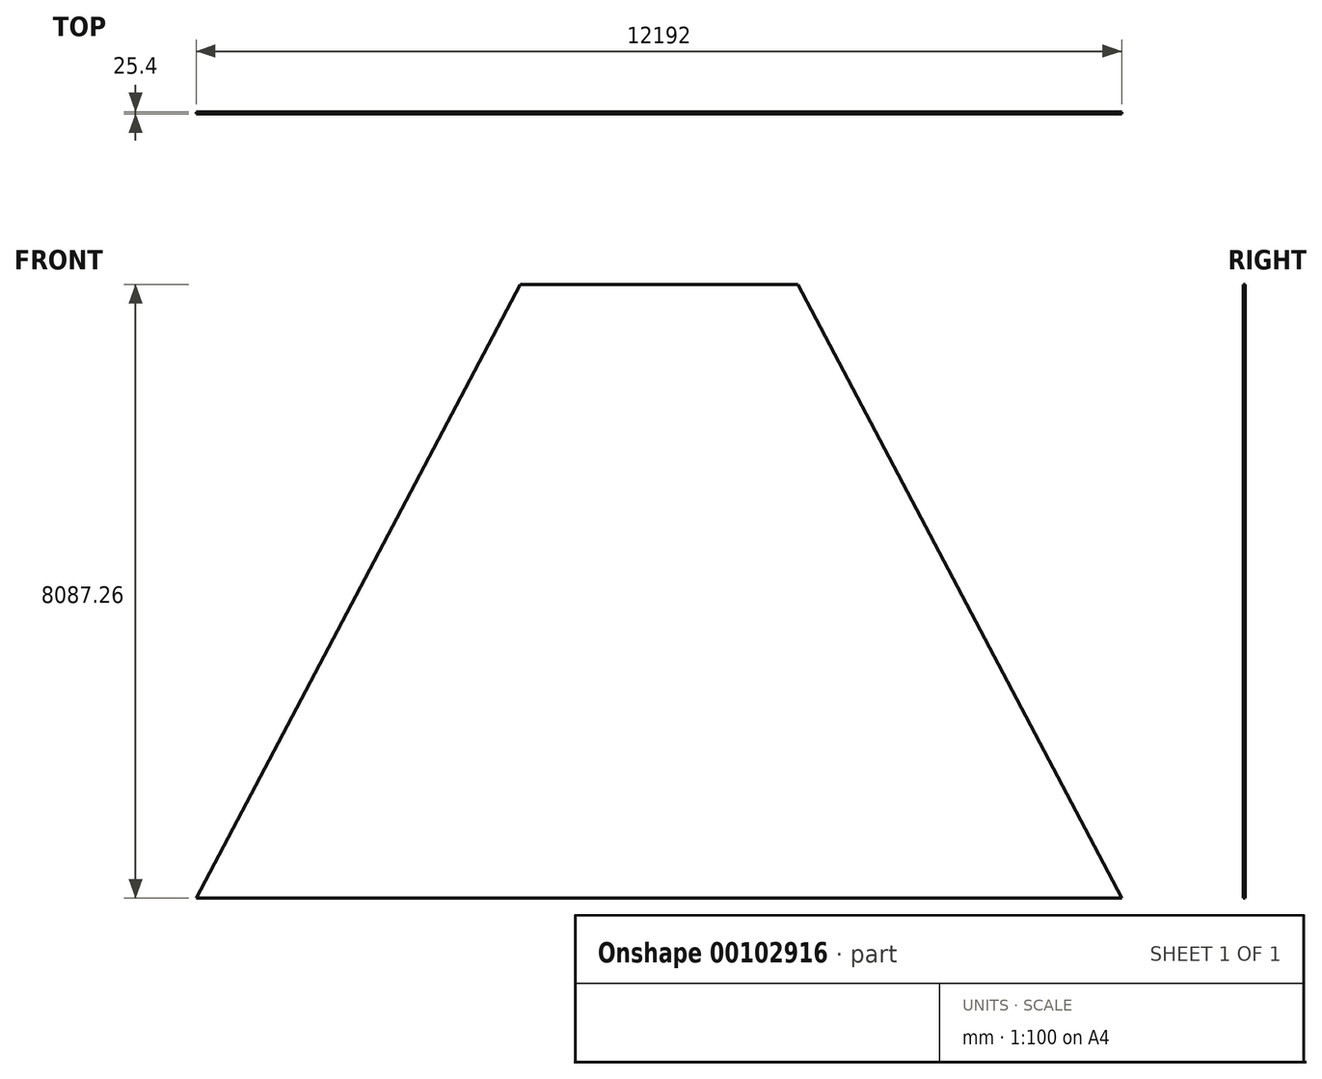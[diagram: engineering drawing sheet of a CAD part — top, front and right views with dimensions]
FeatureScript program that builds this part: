
annotation { "Feature Type Name" : "Feature", "Feature Type Description" : "" }
export const myFeature = defineFeature(function(context is Context, id is Id, definition is map)
    precondition{}
    {
        {
            var Q0;
            Q0=qCreatedBy(makeId("Front.planeOp"),FACE);
            var sketch = newSketch(context, id + "F0", { "sketchPlane" : qUnion([Q0])});
            skLineSegment(sketch, "E0", {"start": v(0, 0) * mm, "end": v(12192, 0) * mm});
            skLineSegment(sketch, "E1", {"start": v(12192, 0) * mm, "end": v(7924.8, 8087.26) * mm});
            skLineSegment(sketch, "E2", {"start": v(7924.8, 8087.26) * mm, "end": v(4267.2, 8087.26) * mm});
            skLineSegment(sketch, "E3", {"start": v(4267.2, 8087.26) * mm, "end": v(0, 0) * mm});
            skSolve(sketch);
        }
        {
            var Q0;
            Q0 = qSketchRegion(id + "F0", true);
            extrude(context, id + "F1", {"entities" : qUnion([Q0]), "depth" : 25.4 * mm});
        }
    });
